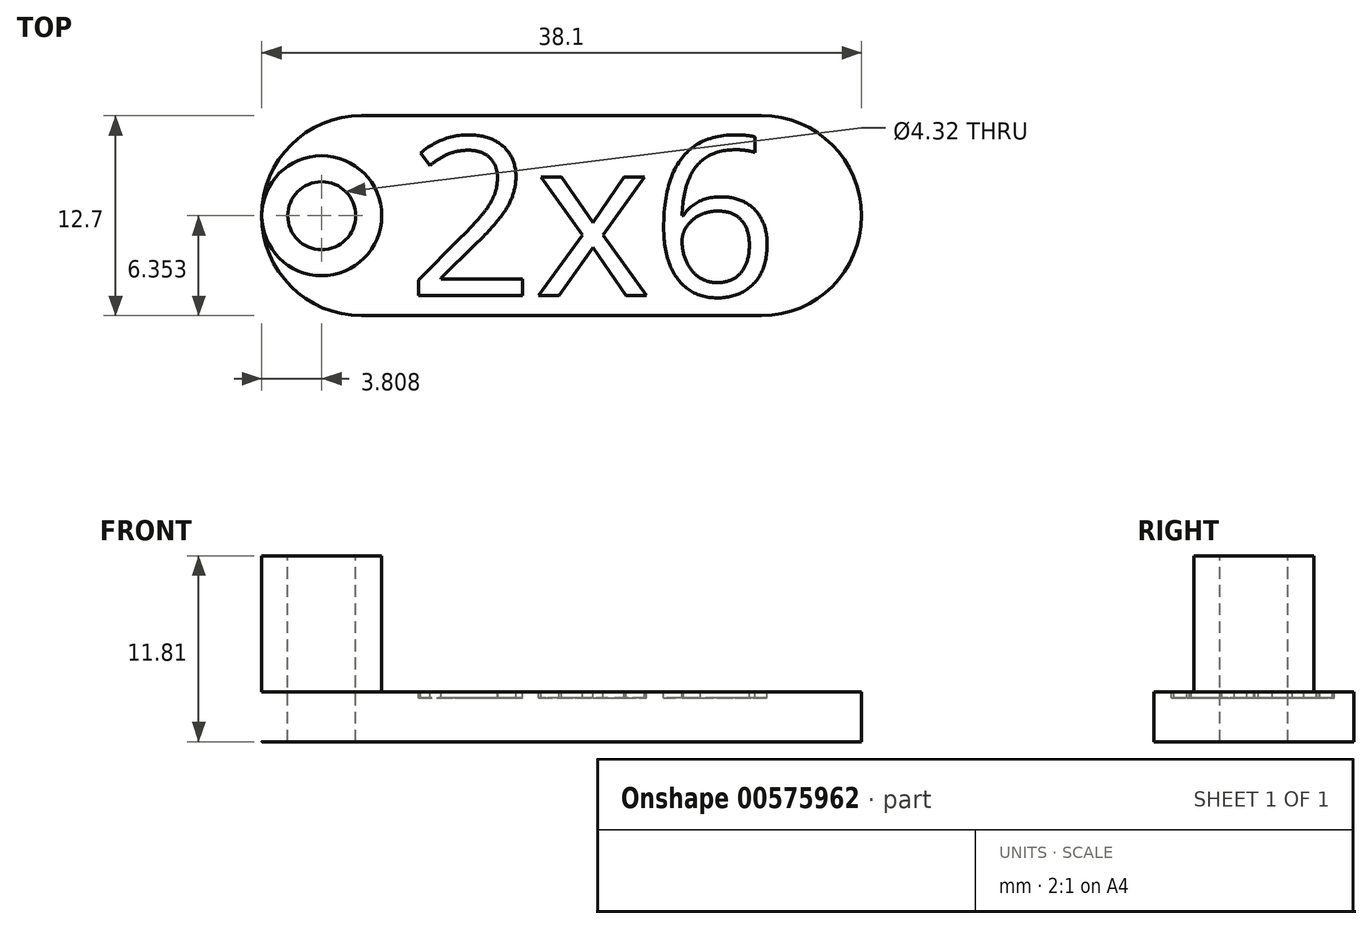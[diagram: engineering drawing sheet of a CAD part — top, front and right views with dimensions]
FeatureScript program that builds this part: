
annotation { "Feature Type Name" : "Feature", "Feature Type Description" : "" }
export const myFeature = defineFeature(function(context is Context, id is Id, definition is map)
    precondition{}
    {
        {
            var Q0;
            Q0=qCreatedBy(makeId("Top.planeOp"),FACE);
            var sketch = newSketch(context, id + "F0", { "sketchPlane" : qUnion([Q0])});
            skLineSegment(sketch, "E0.bottom", {"start": v(-47.46, -10.56) * mm, "end": v(-9.36, -10.56) * mm});
            skLineSegment(sketch, "E0.top", {"start": v(-47.46, -23.26) * mm, "end": v(-9.36, -23.26) * mm});
            skLineSegment(sketch, "E0.left", {"start": v(-47.46, -10.56) * mm, "end": v(-47.46, -23.26) * mm});
            skLineSegment(sketch, "E0.right", {"start": v(-9.36, -10.56) * mm, "end": v(-9.36, -23.26) * mm});
            skSolve(sketch);
        }
        {
            var Q0;
            Q0 = qSketchRegion(id + "F0", true);
            extrude(context, id + "F1", {"entities" : qUnion([Q0]), "depth" : 3.17 * mm, "offsetDistance" : 25.4 * mm, "flatOperationType" : FlatOperationType.REMOVE, "domain" : OperationDomain.MODEL});
        }
        {
            var Q0;
            Q0=makeQuery(id+"F1.opExtrude","CAP_FACE",FACE,{"disambiguationData":[OSD([sQuery(id+"F0.wireOp",EDGE,"E0.bottom"),sQuery(id+"F0.wireOp",EDGE,"E0.top"),sQuery(id+"F0.wireOp",EDGE,"E0.left"),sQuery(id+"F0.wireOp",EDGE,"E0.right")])],"isStart":false});
            var sketch = newSketch(context, id + "F2", { "sketchPlane" : qUnion([Q0])});
            skCircle(sketch, "E1", {"center": v(-43.65, -16.9) * mm, "radius": 3.81 * mm});
            skPoint(sketch, "E1.centerSnap0", {"position": v(-47.46, -16.9) * mm});
            skSolve(sketch);
        }
        {
            var Q0;
            Q0=makeQuery(id+"F2.imprint","IMPRINT",FACE,{"disambiguationData":[TD([[makeQuery(id+"F2.imprint","IMPRINT",EDGE,{"derivedFrom":sQuery(id+"F2.wireOp",EDGE,"E1")}),1.0]])]});
            extrude(context, id + "F3", {"entities" : qUnion([Q0]), "operationType" : NewBodyOperationType.ADD, "depth" : 8.64 * mm, "offsetDistance" : 25.4 * mm});
        }
        {
            var Q0;
            Q0=makeQuery(id+"F3.opExtrude","CAP_FACE",FACE,{"disambiguationData":[OSD([sQuery(id+"F2.wireOp",EDGE,"E1")])],"isStart":false});
            var sketch = newSketch(context, id + "F4", { "sketchPlane" : qUnion([Q0])});
            skCircle(sketch, "E2", {"center": v(-43.65, -16.9) * mm, "radius": 2.16 * mm});
            skSolve(sketch);
        }
        {
            var Q0;
            Q0 = qSketchRegion(id + "F4", true);
            extrude(context, id + "F5", {"entities" : qUnion([Q0]), "operationType" : NewBodyOperationType.REMOVE, "oppositeDirection" : true, "depth" : 25.4 * mm, "offsetDistance" : 25.4 * mm});
        }
        {
            var Q0;
            Q0=makeQuery(id+"F1.opExtrude","SWEPT_EDGE",EDGE,{"disambiguationData":[OSD([sQuery(id+"F0.wireOp",EDGE,"E0.bottom"),sQuery(id+"F0.wireOp",EDGE,"E0.left")])]});
            var Q1;
            Q1=makeQuery(id+"F1.opExtrude","SWEPT_EDGE",EDGE,{"disambiguationData":[OSD([sQuery(id+"F0.wireOp",EDGE,"E0.top"),sQuery(id+"F0.wireOp",EDGE,"E0.left")])]});
            var Q2;
            Q2=makeQuery(id+"F1.opExtrude","SWEPT_EDGE",EDGE,{"disambiguationData":[OSD([sQuery(id+"F0.wireOp",EDGE,"E0.bottom"),sQuery(id+"F0.wireOp",EDGE,"E0.right")])]});
            var Q3;
            Q3=makeQuery(id+"F1.opExtrude","SWEPT_EDGE",EDGE,{"disambiguationData":[OSD([sQuery(id+"F0.wireOp",EDGE,"E0.top"),sQuery(id+"F0.wireOp",EDGE,"E0.right")])]});
            fillet(context, id + "F6", {"entities" : qUnion([Q0, Q1, Q2, Q3]), "radius" : 6.35 * mm, "tangentPropagation" : true, "allowEdgeOverflow" : false});
        }
        {
            var Q0;
            Q0=makeQuery(id+"F1.opExtrude","CAP_FACE",FACE,{"disambiguationData":[OSD([sQuery(id+"F0.wireOp",EDGE,"E0.bottom"),sQuery(id+"F0.wireOp",EDGE,"E0.top"),sQuery(id+"F0.wireOp",EDGE,"E0.left"),sQuery(id+"F0.wireOp",EDGE,"E0.right")])],"isStart":false});
            var sketch = newSketch(context, id + "F7", { "sketchPlane" : qUnion([Q0])});
            skText(sketch, "E3", { "text": "2x6", "fontName": "OpenSans-Regular.ttf"});
            const initialGuessF7  = {"E3": [-0.0382, -0.02199, 1, 0, 0.01016]};
            skSetInitialGuess(sketch, initialGuessF7);
            skSolve(sketch);
        }
        {
            var Q0;
            Q0 = qSketchRegion(id + "F7", true);
            extrude(context, id + "F8", {"entities" : qUnion([Q0]), "operationType" : NewBodyOperationType.REMOVE, "oppositeDirection" : true, "depth" : 0.38 * mm, "offsetDistance" : 25.4 * mm});
        }
    });
